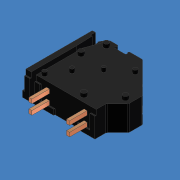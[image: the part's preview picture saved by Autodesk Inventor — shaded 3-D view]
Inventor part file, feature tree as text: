
AUTODESK INVENTOR PART (.ipt)
format: ipt  version: 2012 (Build 160160000, 160)  size: 269,824 bytes
history: native  units: mm (DEFAULTED — no unit token found)
features: sketch x21, extrude x18, revolve x2, pattern_linear x2
ambient origin geometry x8: Origin, YZ Plane, XZ Plane, XY Plane, X Axis, Y Axis, Z Axis, Center Point
bodies: Solid1 (feature_tree)
feature tree (43):
  extrude  "Extrusion1"  Depth=10.0mm TaperAngle=0.0deg
  extrude  "Extrusion2"  Depth=8.8mm TaperAngle=0.0deg
  extrude  "Extrusion3"  Depth=1.5mm TaperAngle=0.0deg
  extrude  "Extrusion4"  Depth=1.5mm TaperAngle=0.0deg
  extrude  "Extrusion5"  Depth=1.5mm TaperAngle=0.0deg
  extrude  "Extrusion6"  Depth=1.5mm TaperAngle=0.0deg
  extrude  "Extrusion7"  Depth=6.3mm TaperAngle=0.0deg
  extrude  "Extrusion8"  TaperAngle=360.0deg  [1 undecoded]
  extrude  "Extrusion9"  TaperAngle=360.0deg  [1 undecoded]
  extrude  "Extrusion10"  Depth=20.0mm TaperAngle=0.0deg
  extrude  "Extrusion11"  Depth=20.0mm TaperAngle=0.0deg
  extrude  "Extrusion12"  [1 undecoded]
  extrude  "Extrusion13"  [1 undecoded]
  extrude  "Extrusion14"  [1 undecoded]
  extrude  "Extrusion15"  [1 undecoded]
  revolve  "Revolution1"  [1 undecoded]
  extrude  "Extrusion16"  [1 undecoded]
  revolve  "Revolution2"  [1 undecoded]
  extrude  "Extrusion17"  [1 undecoded]
  pattern_linear  "Rectangular Pattern1"  [2 undecoded]
  extrude  "Extrusion18"  [1 undecoded]
  pattern_linear  "Rectangular Pattern2"  [2 undecoded]
  sketch  "Sketch21"
  sketch  "Skizze_1"  dims[d0=10.0mm d1=0.0mm d2=10.0mm d3=0.0mm]
  sketch  "Skizze_2"  dims[d4=2.4mm d5=0.0mm d6=8.8mm d7=0.0mm]
  sketch  "Skizze_4"  dims[d12=1.5mm d13=0.0mm d14=1.5mm d15=0.0mm]
  sketch  "Skizze_3"  dims[d8=7.6mm d9=0.0mm d10=1.5mm d11=0.0mm]
  sketch  "Skizze_5"  dims[d16=1.5mm d17=0.0mm d18=1.5mm d19=0.0mm]
  sketch  "Skizze_8"  dims[d28=0.5mm d29=0.0mm d30=360.0deg]
  sketch  "Skizze_9"  dims[d31=6.5mm d32=0.0mm d33=360.0deg]
  sketch  "Skizze_10"  dims[d34=13.0mm d35=0.0mm d36=20.0mm d38=15.0mm d39=10.0mm d41=0.0mm]
  sketch  "Skizze_11"  dims[d42=13.0mm d43=0.0mm d44=20.0mm d46=15.0mm d47=10.0mm d49=0.0mm]
  sketch  "Skizze_12"
  sketch  "Skizze_13"
  sketch  "Skizze_14"
  sketch  "Skizze_15"
  sketch  "Skizze_6"  dims[d20=1.5mm d21=0.0mm d22=1.5mm d23=0.0mm]
  sketch  "Skizze_7"  dims[d24=1.5mm d25=0.0mm d26=6.3mm d27=0.0mm]
  sketch  "Skizze_16"
  sketch  "Skizze_17"
  sketch  "Skizze_18"
  sketch  "Skizze_19"
  sketch  "Skizze_21"
note: 15 required parameter values undecoded (feature->parameter linkage not recoverable at this tier; creation-order binding heuristic only, values carry confidence <= 0.55)
